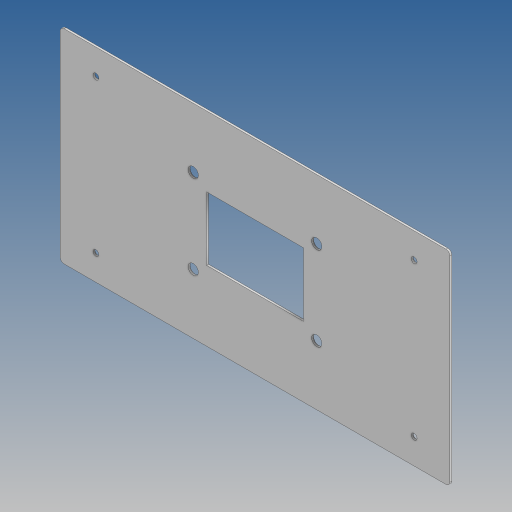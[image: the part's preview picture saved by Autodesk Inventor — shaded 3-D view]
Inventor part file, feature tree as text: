
AUTODESK INVENTOR PART (.ipt)
format: ipt  version: 2023.3 (Build 273359000, 359)  size: 142,336 bytes
history: native  units: mm
features: sketch x4, extrude x2, hole x2, fillet x1
ambient origin geometry x8: Origin, YZ Plane, XZ Plane, XY Plane, X Axis, Y Axis, Z Axis, Center Point
bodies: Volumenkörper1 (feature_tree)
feature tree (9):
  extrude  "Extrusion1"  Depth=1.5mm
  hole  "Bohrung1"  [1 undecoded]
  fillet  "Rundung1"  Radius=160.0mm
  extrude  "Extrusion2"  Depth=153.0mm
  hole  "Bohrung2"  [1 undecoded]
  sketch  "Skizze1"  dims[d0=306.0mm d1=1.5mm]
  sketch  "Skizze2"  dims[d2=160.0mm d3=0.0mm d4=306.0mm d5=160.0mm]
  sketch  "Skizze3"  dims[d6=153.0mm d7=80.0mm]
  sketch  "Skizze4"  dims[d8=250.0mm d9=120.0mm d10=4.5mm d11=6.0mm d12=4.0mm d13=2.0mm d14=90.0deg d15=11.8mm d16=20.594885mm d17=3.0mm d18=76.0mm d19=50.0mm d20=0.0mm d21=0.0mm d22=97.0mm d23=66.0mm d24=8.0mm d25=6.0mm d26=4.0mm d27=2.0mm d28=90.0deg d29=8.0mm d30=20.594885mm]
note: 2 required parameter values undecoded (feature->parameter linkage not recoverable at this tier; creation-order binding heuristic only, values carry confidence <= 0.55)
